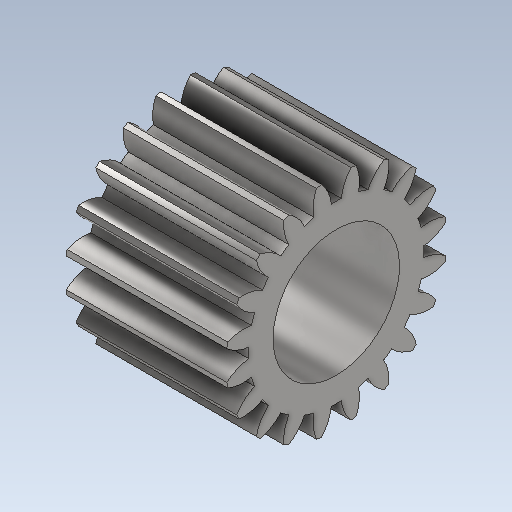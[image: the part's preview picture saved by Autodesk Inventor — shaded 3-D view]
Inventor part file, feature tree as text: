
AUTODESK INVENTOR PART (.ipt)
format: ipt  version: 2023 (Build 270158000, 158)  size: 590,336 bytes
history: native  units: in
note: dims shown in document units (in); Inventor stores cm internally (conversion verified against a paired STEP export)
features: extrude x2, sketch x2, other x1
ambient origin geometry x8: Origin, YZ Plane, XZ Plane, XY Plane, X Axis, Y Axis, Z Axis, Center Point
bodies: Solid1 (feature_tree)
feature tree (5):
  extrude  "Extrusion1"  TaperAngle=0.0deg  [1 undecoded]
  extrude  "Extrusion2"  TaperAngle=0.0deg  [1 undecoded]
  sketch  "Sketch1"  dims[d0=0.5in d1=0.0in d2=0.0in]
  sketch  "Sketch2"  dims[d4=0.3937in d5=0.0in d6=0.0in]
  other  "TeethCuts"
note: 2 required parameter values undecoded (feature->parameter linkage not recoverable at this tier; creation-order binding heuristic only, values carry confidence <= 0.55)
